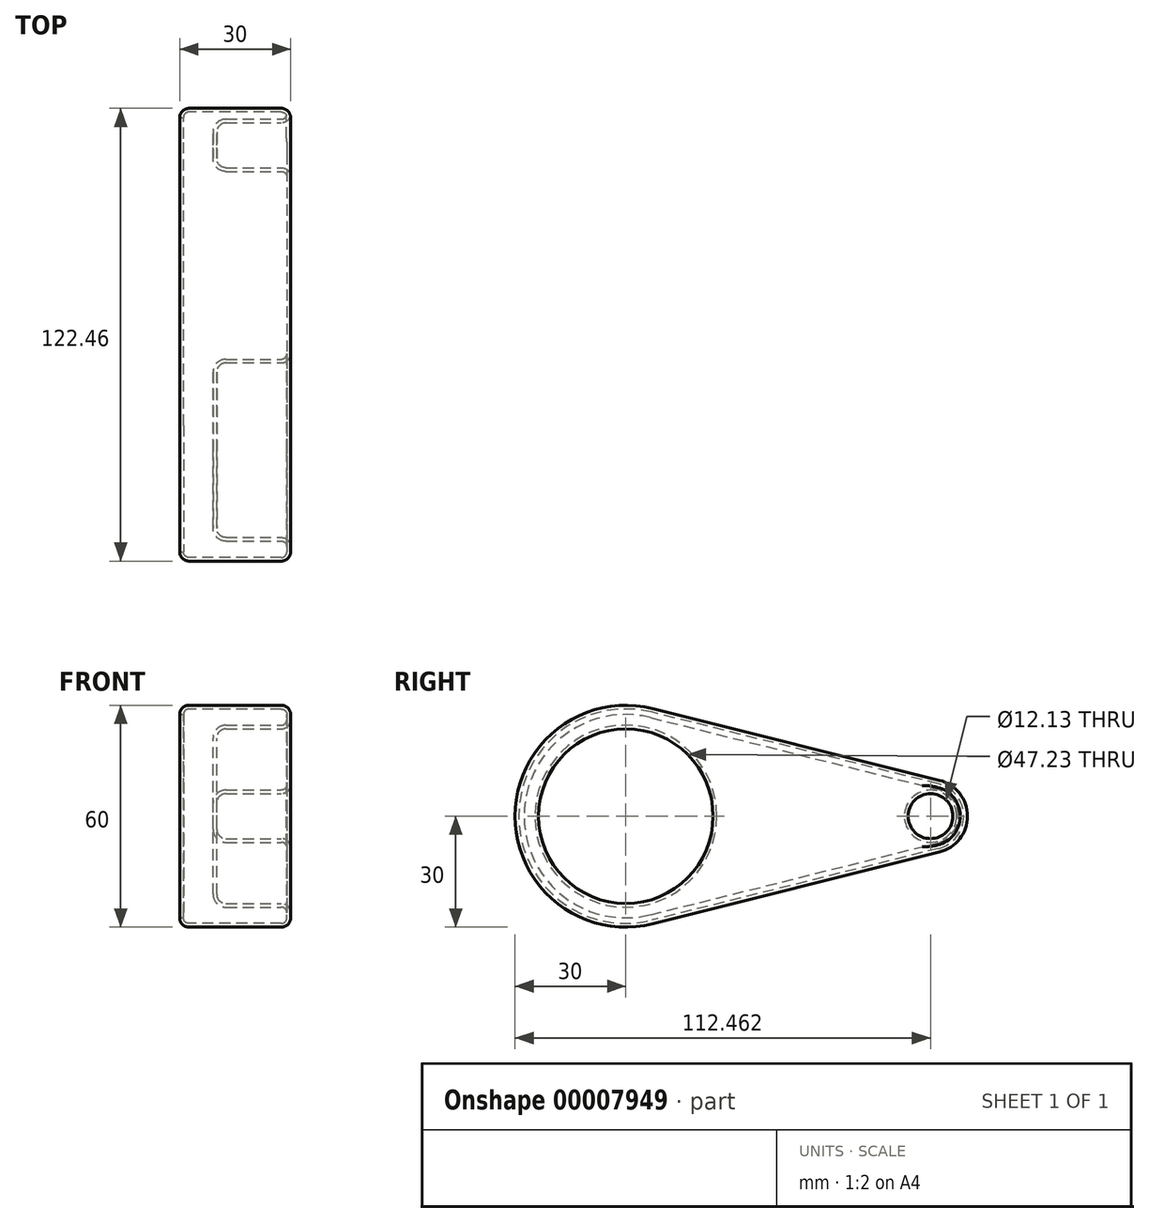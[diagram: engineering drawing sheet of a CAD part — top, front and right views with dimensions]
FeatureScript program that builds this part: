
annotation { "Feature Type Name" : "Feature", "Feature Type Description" : "" }
export const myFeature = defineFeature(function(context is Context, id is Id, definition is map)
    precondition{}
    {
        {
            var Q0;
            Q0=qCreatedBy(makeId("Right.planeOp"),FACE);
            var sketch = newSketch(context, id + "F0", { "sketchPlane" : qUnion([Q0])});
            skCircle(sketch, "E0", {"center": v(0, 0) * mm, "radius": 30 * mm});
            skCircle(sketch, "E1", {"center": v(82.46, 0) * mm, "radius": 10 * mm});
            skLineSegment(sketch, "E2", {"start": v(7.28, 29.1) * mm, "end": v(84.89, 9.7) * mm});
            skLineSegment(sketch, "E3", {"start": v(7.28, -29.1) * mm, "end": v(84.89, -9.7) * mm});
            skSolve(sketch);
        }
        {
            var Q0;
            Q0 = qSketchRegion(id + "F0", true);
            extrude(context, id + "F1", {"entities" : qUnion([Q0]), "depth" : 30 * mm});
        }
        {
            var Q0;
            Q0=makeQuery(id+"F1.opExtrude","CAP_FACE",FACE,{"disambiguationData":[OSD([sQuery(id+"F0.wireOp",EDGE,"E0"),sQuery(id+"F0.wireOp",EDGE,"E1"),sQuery(id+"F0.wireOp",EDGE,"E2"),sQuery(id+"F0.wireOp",EDGE,"E3")])],"isStart":false});
            var sketch = newSketch(context, id + "F2", { "sketchPlane" : qUnion([Q0])});
            skCircle(sketch, "E4", {"center": v(0, 0) * mm, "radius": 23.62 * mm});
            skCircle(sketch, "E5", {"center": v(82.46, 0) * mm, "radius": 6.07 * mm});
            skSolve(sketch);
        }
        {
            var Q0;
            Q0=makeQuery(id+"F2.imprint","IMPRINT",FACE,{"disambiguationData":[TD([[makeQuery(id+"F2.imprint","IMPRINT",EDGE,{"derivedFrom":sQuery(id+"F2.wireOp",EDGE,"E4")}),1.0]])]});
            var Q1;
            Q1=makeQuery(id+"F2.imprint","IMPRINT",FACE,{"disambiguationData":[TD([[makeQuery(id+"F2.imprint","IMPRINT",EDGE,{"derivedFrom":sQuery(id+"F2.wireOp",EDGE,"E5")}),1.0]])]});
            extrude(context, id + "F3", {"entities" : qUnion([Q0, Q1]), "operationType" : NewBodyOperationType.REMOVE, "oppositeDirection" : true, "depth" : 20 * mm});
        }
        {
            var Q0;
            Q0=makeQuery(id+"F1.opExtrude","CAP_FACE",FACE,{"disambiguationData":[OSD([sQuery(id+"F0.wireOp",EDGE,"E0"),sQuery(id+"F0.wireOp",EDGE,"E1"),sQuery(id+"F0.wireOp",EDGE,"E2"),sQuery(id+"F0.wireOp",EDGE,"E3")])],"isStart":false});
            var Q1;
            Q1=makeQuery(id+"F1.opExtrude","CAP_EDGE",EDGE,{"disambiguationData":[OSD([sQuery(id+"F0.wireOp",EDGE,"E0")])],"isStart":true});
            var Q2;
            Q2=makeQuery(id+"F3.boolean.opBoolean","COPY",FACE,{"derivedFrom":makeQuery(id+"F3.opExtrude","CAP_FACE",FACE,{"disambiguationData":[OSD([sQuery(id+"F2.wireOp",EDGE,"E4")])],"isStart":false})});
            var Q3;
            Q3=makeQuery(id+"F3.boolean.opBoolean","COPY",FACE,{"derivedFrom":makeQuery(id+"F3.opExtrude","CAP_FACE",FACE,{"disambiguationData":[OSD([sQuery(id+"F2.wireOp",EDGE,"E5")])],"isStart":false})});
            fillet(context, id + "F4", {"entities" : qUnion([Q0, Q1, Q2, Q3]), "radius" : 2.5 * mm, "tangentPropagation" : true, "allowEdgeOverflow" : false});
        }
        {
            var Q0;
            Q0=makeQuery(id+"F1.opExtrude","CAP_FACE",FACE,{"disambiguationData":[OSD([sQuery(id+"F0.wireOp",EDGE,"E0"),sQuery(id+"F0.wireOp",EDGE,"E1"),sQuery(id+"F0.wireOp",EDGE,"E2"),sQuery(id+"F0.wireOp",EDGE,"E3")])],"isStart":true});
            shell(context, id + "F5", {"entities" : qUnion([Q0]), "thickness" : 1 * mm});
        }
    });
